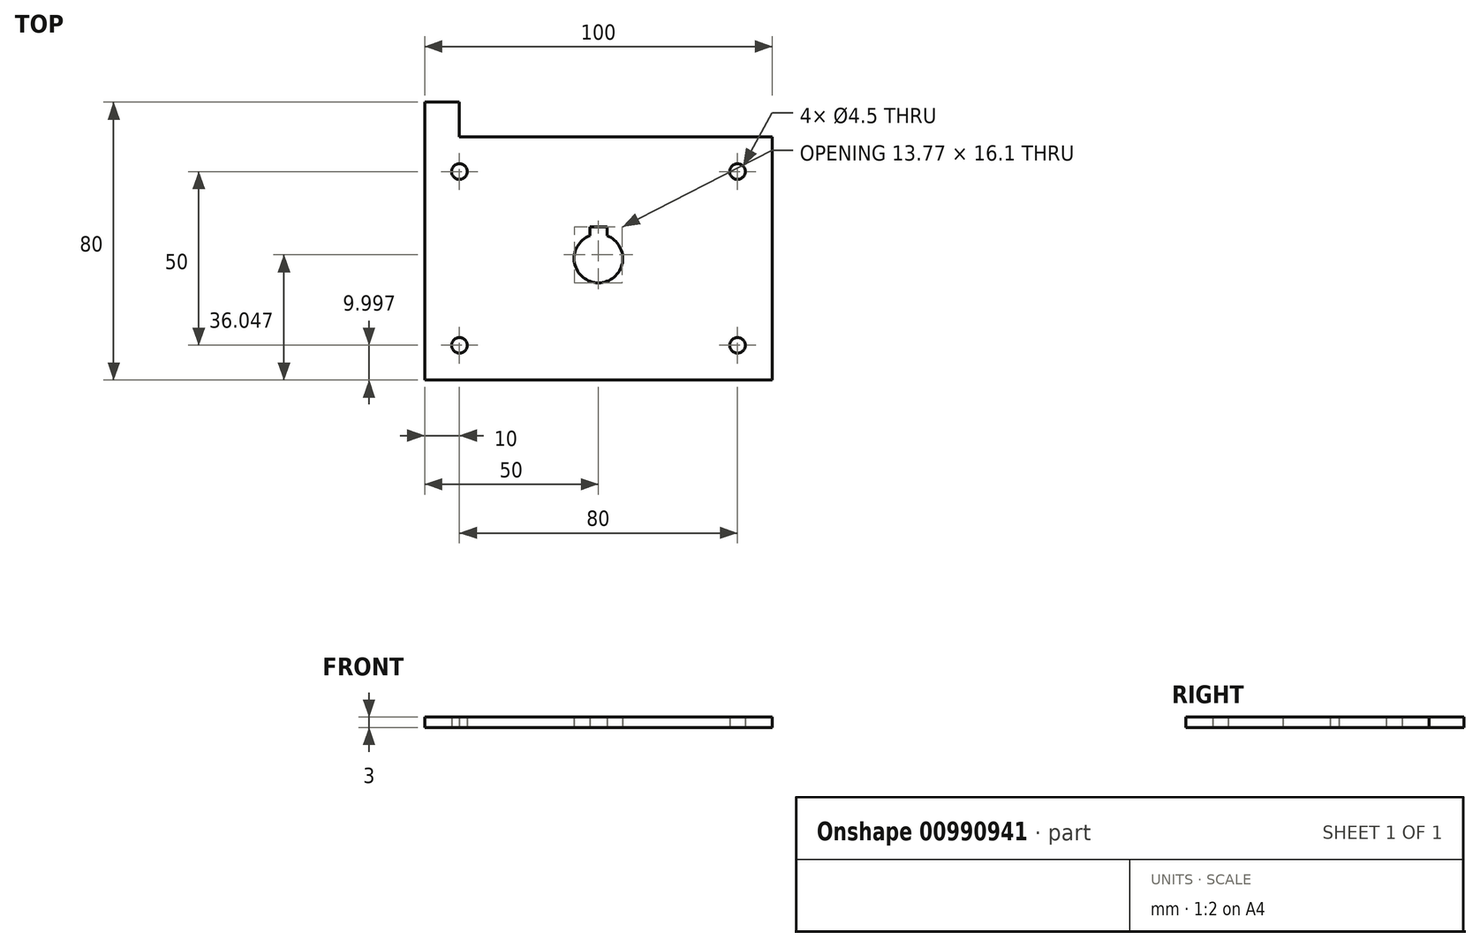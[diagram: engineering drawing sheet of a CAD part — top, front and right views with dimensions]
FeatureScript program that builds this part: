
annotation { "Feature Type Name" : "Feature", "Feature Type Description" : "" }
export const myFeature = defineFeature(function(context is Context, id is Id, definition is map)
    precondition{}
    {
        {
            var Q0;
            Q0=qCreatedBy(makeId("Top.planeOp"),FACE);
            var sketch = newSketch(context, id + "F0", { "sketchPlane" : qUnion([Q0])});
            skLineSegment(sketch, "E0", {"start": v(2.5, 1.57) * mm, "end": v(2.5, 4.13) * mm});
            skLineSegment(sketch, "E1", {"start": v(2.5, 4.13) * mm, "end": v(-2.5, 4.13) * mm});
            skLineSegment(sketch, "E2", {"start": v(-2.5, 4.13) * mm, "end": v(-2.5, 1.57) * mm});
            skCircle(sketch, "E3.converted", {"center": v(0, -4.97) * mm, "radius": 7 * mm});
            skPoint(sketch, "E4", {"position": v(0, 2.03) * mm});
            skLineSegment(sketch, "E5.bottom", {"start": v(50, -39.97) * mm, "end": v(-50, -39.97) * mm});
            skLineSegment(sketch, "E5.top", {"start": v(-40, 40.03) * mm, "end": v(-50, 40.03) * mm});
            skLineSegment(sketch, "E5.left", {"start": v(50, -39.97) * mm, "end": v(50, 30.03) * mm});
            skLineSegment(sketch, "E5.right", {"start": v(-50, -39.97) * mm, "end": v(-50, 40.03) * mm});
            skLineSegment(sketch, "E6", {"start": v(-50, 30.03) * mm, "end": v(50, 30.03) * mm});
            skLineSegment(sketch, "E7", {"start": v(-40, 40.03) * mm, "end": v(-40, 30.03) * mm});
            skPoint(sketch, "E8.orphan", {"position": v(50, 40.03) * mm});
            skLineSegment(sketch, "E9", {"start": v(-50, -39.97) * mm, "end": v(-50, 30.03) * mm});
            skPoint(sketch, "E10", {"position": v(-50, 20.03) * mm});
            skPoint(sketch, "E11", {"position": v(40, 20.03) * mm});
            skPoint(sketch, "E12", {"position": v(40, -29.97) * mm});
            skPoint(sketch, "E13", {"position": v(-50, -29.97) * mm});
            skCircle(sketch, "E14", {"center": v(40, 20.03) * mm, "radius": 2.25 * mm});
            skCircle(sketch, "E15.MirrorC", {"center": v(40, -29.97) * mm, "radius": 2.25 * mm});
            skCircle(sketch, "E16.MirrorC", {"center": v(-40, 20.03) * mm, "radius": 2.25 * mm});
            skCircle(sketch, "E17.MirrorC", {"center": v(-40, -29.97) * mm, "radius": 2.25 * mm});
            skSolve(sketch);
        }
        {
            var Q0;
            {var subQ7=sQuery(id+"F0.wireOp",EDGE,"E0");Q0=makeQuery(id+"F0.imprint","IMPRINT",FACE,{"disambiguationData":[TD([[makeQuery(id+"F0.imprint","IMPRINT",EDGE,{"derivedFrom":subQ7}),-1.0]])]});}
            var Q1;
            {var subQ5=sQuery(id+"F0.wireOp",EDGE,"4xxc5oVe-U1D8-RdDk-WCKI-GAU98GmUnVuJ");var subQ6=sQuery(id+"F0.wireOp",EDGE,"E5.bottom");var subQ7=makeQuery(id+"F0.imprint","INTERSECT",VERTEX,{"derivedFrom":[subQ6,subQ5]});Q1=makeQuery(id+"F0.imprint","IMPRINT",FACE,{"disambiguationData":[TD([[makeQuery(id+"F0.imprint","IMPRINT",EDGE,{"disambiguationData":[TD([[subQ7,-1.0]])],"derivedFrom":subQ6}),-1.0]])]});}
            var Q2;
            {var subQ5=sQuery(id+"F0.wireOp",EDGE,"4xxc5oVe-U1D8-RdDk-WCKI-GAU98GmUnVuJ");var subQ6=sQuery(id+"F0.wireOp",EDGE,"E5.bottom");var subQ7=makeQuery(id+"F0.imprint","INTERSECT",VERTEX,{"derivedFrom":[subQ6,subQ5]});Q2=makeQuery(id+"F0.imprint","IMPRINT",FACE,{"disambiguationData":[TD([[makeQuery(id+"F0.imprint","IMPRINT",EDGE,{"disambiguationData":[TD([[subQ7,1.0]])],"derivedFrom":subQ6}),-1.0]])]});}
            var Q3;
            {var subQ0=sQuery(id+"F0.wireOp",EDGE,"4jpTKrsM-aKTq-Esgq-MGsV-NbsFvEdi3Mff");var subQ5=sQuery(id+"F0.wireOp",EDGE,"E5.left");var subQ6=makeQuery(id+"F0.imprint","INTERSECT",VERTEX,{"derivedFrom":[subQ5,subQ0]});Q3=makeQuery(id+"F0.imprint","IMPRINT",FACE,{"disambiguationData":[TD([[makeQuery(id+"F0.imprint","IMPRINT",EDGE,{"disambiguationData":[TD([[subQ6,1.0]])],"derivedFrom":subQ5}),1.0]])]});}
            var Q4;
            {var subQ0=sQuery(id+"F0.wireOp",EDGE,"4jpTKrsM-aKTq-Esgq-MGsV-NbsFvEdi3Mff");var subQ1=sQuery(id+"F0.wireOp",EDGE,"E5.left");var subQ2=makeQuery(id+"F0.imprint","INTERSECT",VERTEX,{"derivedFrom":[subQ1,subQ0]});Q4=makeQuery(id+"F0.imprint","IMPRINT",FACE,{"disambiguationData":[TD([[makeQuery(id+"F0.imprint","IMPRINT",EDGE,{"disambiguationData":[TD([[subQ2,-1.0]])],"derivedFrom":subQ1}),1.0]])]});}
            var Q5;
            {var subQ1=sQuery(id+"F0.wireOp",EDGE,"E6");var subQ6=sQuery(id+"F0.wireOp",EDGE,"E5.left");var subQ9=makeQuery(id+"F0.imprint","INTERSECT",VERTEX,{"derivedFrom":[subQ6,subQ1]});Q5=makeQuery(id+"F0.imprint","IMPRINT",FACE,{"disambiguationData":[TD([[makeQuery(id+"F0.imprint","IMPRINT",EDGE,{"disambiguationData":[TD([[subQ9,1.0]])],"derivedFrom":subQ6}),1.0]])]});}
            var Q6;
            {var subQ1=sQuery(id+"F0.wireOp",EDGE,"FJSjo2PN-oite-CpyQ-YUBK-05txENasCkpn");var subQ8=sQuery(id+"F0.wireOp",EDGE,"E5.right");var subQ12=makeQuery(id+"F0.imprint","INTERSECT",VERTEX,{"derivedFrom":[subQ8,subQ1]});Q6=makeQuery(id+"F0.imprint","IMPRINT",FACE,{"disambiguationData":[TD([[makeQuery(id+"F0.imprint","IMPRINT",EDGE,{"disambiguationData":[TD([[subQ12,-1.0]])],"derivedFrom":subQ8}),-1.0]])]});}
            var Q7;
            {var subQ0=sQuery(id+"F0.wireOp",EDGE,"E5.top");Q7=makeQuery(id+"F0.imprint","IMPRINT",FACE,{"disambiguationData":[TD([[makeQuery(id+"F0.imprint","IMPRINT",EDGE,{"derivedFrom":subQ0}),1.0]])]});}
            extrude(context, id + "F1", {"entities" : qUnion([Q0, Q1, Q2, Q3, Q4, Q5, Q6, Q7]), "depth" : 3 * mm, "offsetDistance" : 25 * mm});
        }
    });
